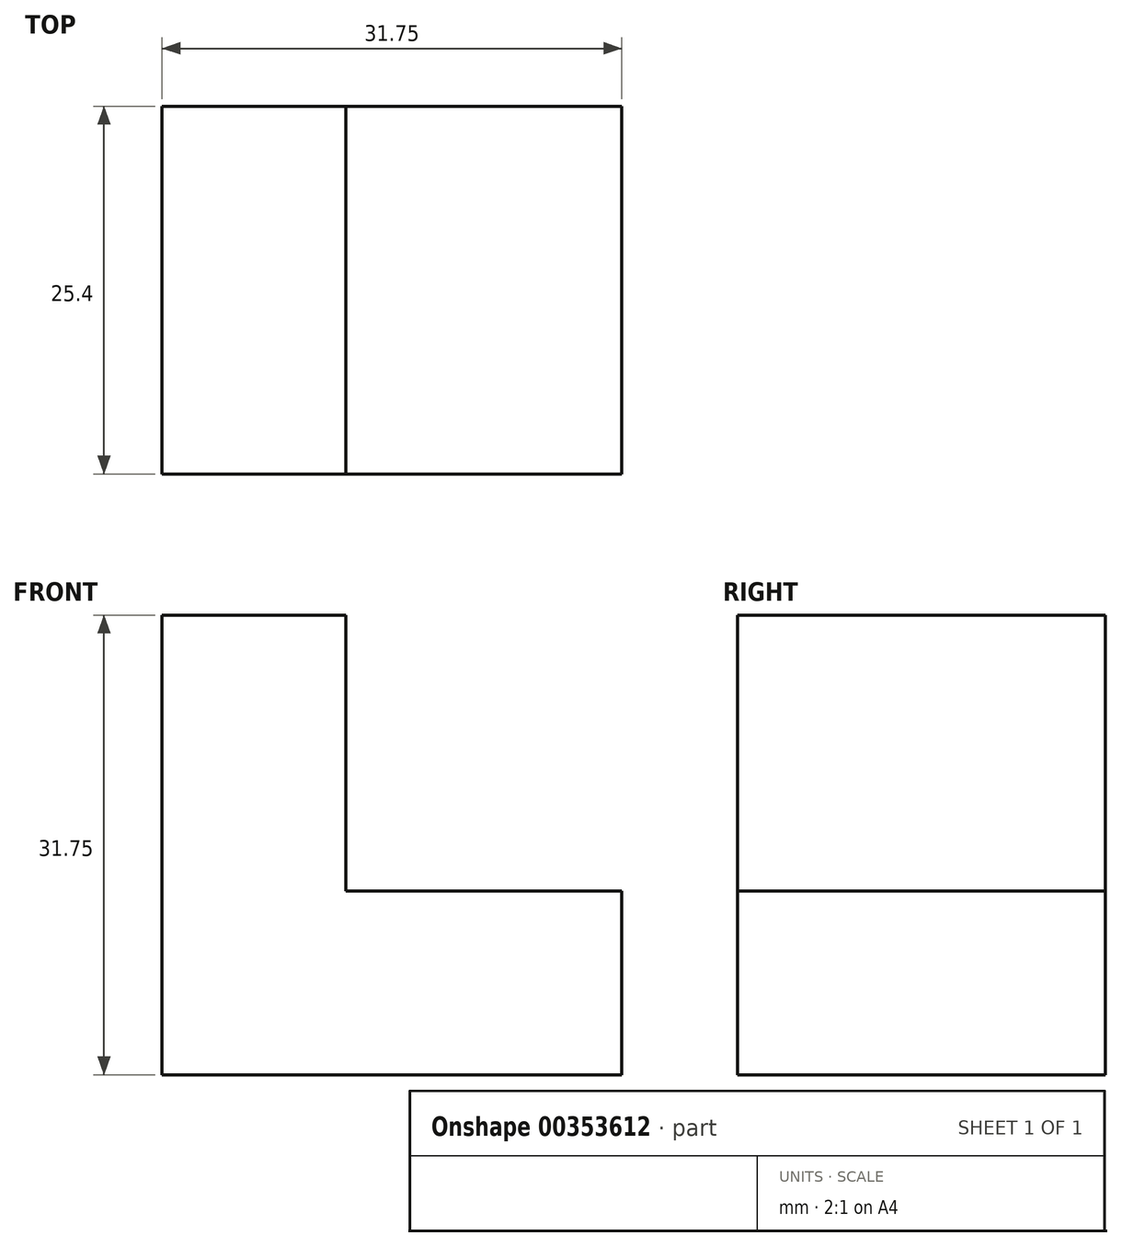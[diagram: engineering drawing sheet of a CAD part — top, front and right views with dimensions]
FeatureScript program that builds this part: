
annotation { "Feature Type Name" : "Feature", "Feature Type Description" : "" }
export const myFeature = defineFeature(function(context is Context, id is Id, definition is map)
    precondition{}
    {
        {
            var Q0;
            Q0=qCreatedBy(makeId("Front.planeOp"),FACE);
            var sketch = newSketch(context, id + "F0", { "sketchPlane" : qUnion([Q0])});
            skLineSegment(sketch, "E0", {"start": v(0, 0) * mm, "end": v(0, 31.75) * mm});
            skLineSegment(sketch, "E1", {"start": v(0, 31.75) * mm, "end": v(12.7, 31.75) * mm});
            skLineSegment(sketch, "E2", {"start": v(12.7, 31.75) * mm, "end": v(12.7, 12.7) * mm});
            skLineSegment(sketch, "E3", {"start": v(12.7, 12.7) * mm, "end": v(31.75, 12.7) * mm});
            skLineSegment(sketch, "E4", {"start": v(31.75, 12.7) * mm, "end": v(31.75, 0) * mm});
            skLineSegment(sketch, "E5", {"start": v(31.75, 0) * mm, "end": v(0, 0) * mm});
            skSolve(sketch);
        }
        {
            var Q0;
            Q0 = qSketchRegion(id + "F0", true);
            extrude(context, id + "F1", {"entities" : qUnion([Q0]), "depth" : 25.4 * mm});
        }
    });
